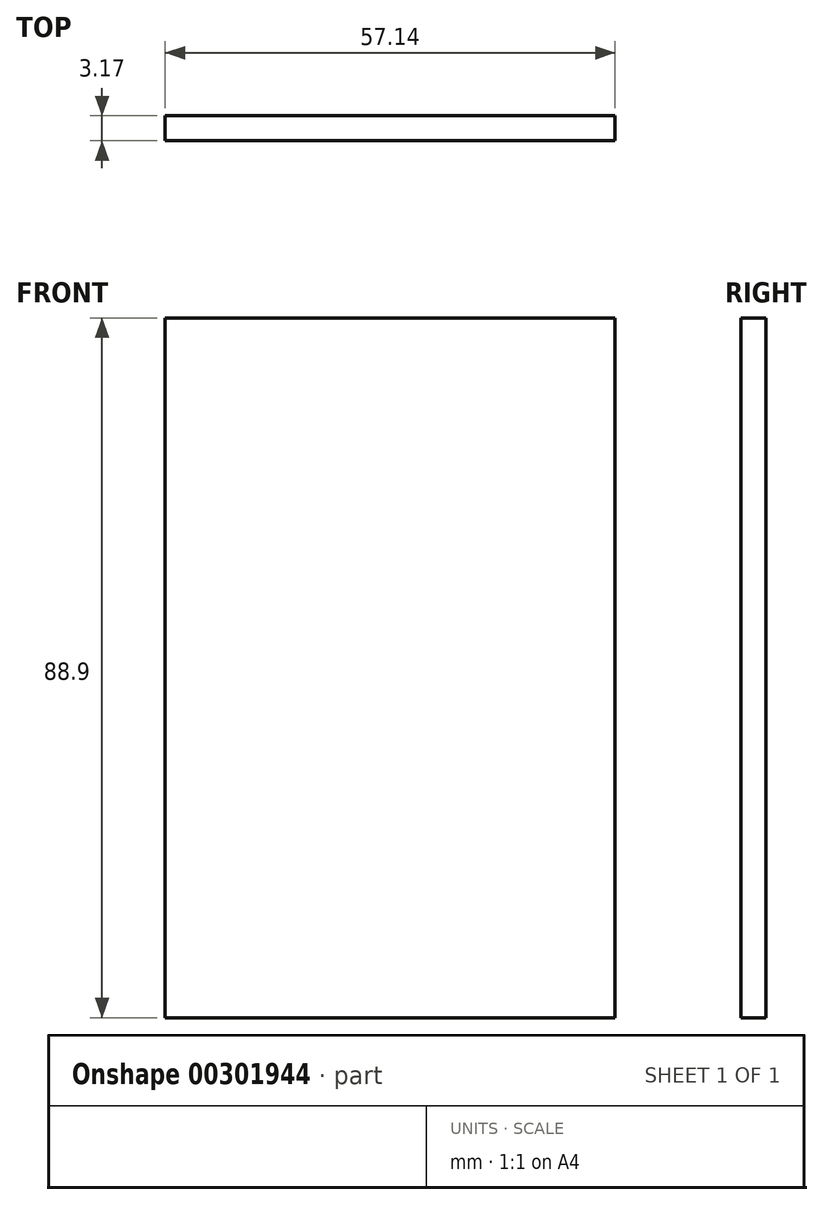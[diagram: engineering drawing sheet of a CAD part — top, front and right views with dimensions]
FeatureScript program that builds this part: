
annotation { "Feature Type Name" : "Feature", "Feature Type Description" : "" }
export const myFeature = defineFeature(function(context is Context, id is Id, definition is map)
    precondition{}
    {
        {
            var Q0;
            Q0=qCreatedBy(makeId("Front.planeOp"),FACE);
            var sketch = newSketch(context, id + "F0", { "sketchPlane" : qUnion([Q0])});
            skLineSegment(sketch, "E0.bottom", {"start": v(-28.57, 44.45) * mm, "end": v(28.58, 44.45) * mm});
            skLineSegment(sketch, "E0.top", {"start": v(-28.58, -44.45) * mm, "end": v(28.57, -44.45) * mm});
            skLineSegment(sketch, "E0.left", {"start": v(-28.57, 44.45) * mm, "end": v(-28.58, -44.45) * mm});
            skLineSegment(sketch, "E0.right", {"start": v(28.58, 44.45) * mm, "end": v(28.57, -44.45) * mm});
            skPoint(sketch, "E0.middle", {"position": v(0, 0) * mm});
            skSolve(sketch);
        }
        {
            var Q0;
            Q0=makeQuery(id+"F0.imprint","IMPRINT",FACE,{"disambiguationData":[TD([[makeQuery(id+"F0.imprint","IMPRINT",EDGE,{"derivedFrom":sQuery(id+"F0.wireOp",EDGE,"E0.bottom")}),-1.0]])]});
            extrude(context, id + "F1", {"entities" : qUnion([Q0]), "depth" : 3.17 * mm});
        }
    });
